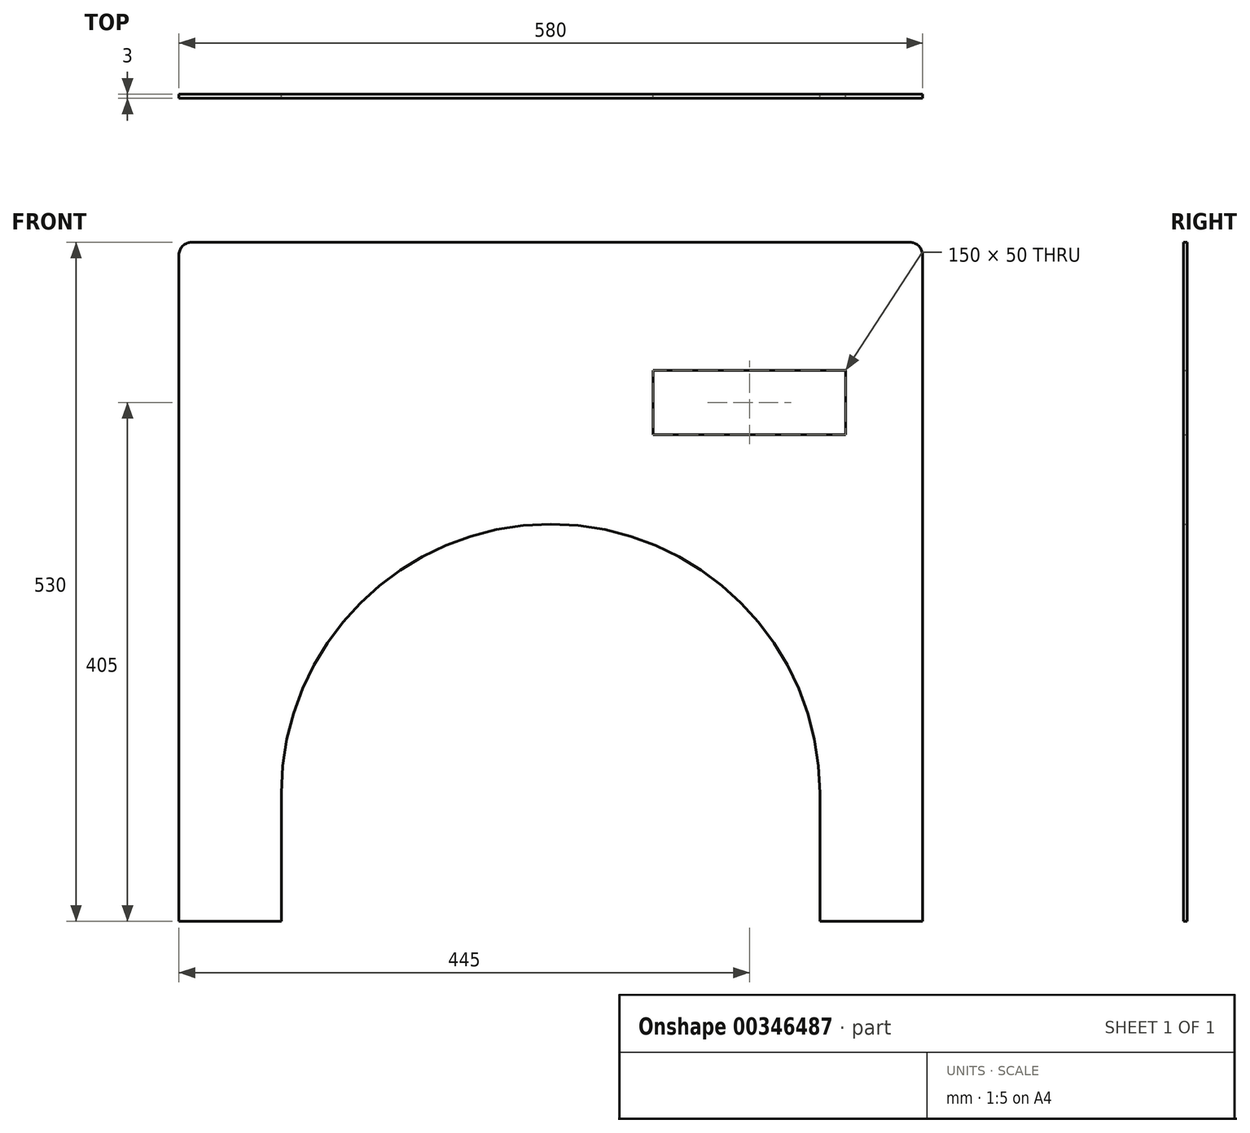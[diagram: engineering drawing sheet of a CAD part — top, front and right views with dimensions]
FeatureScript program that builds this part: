
annotation { "Feature Type Name" : "Feature", "Feature Type Description" : "" }
export const myFeature = defineFeature(function(context is Context, id is Id, definition is map)
    precondition{}
    {
        {
            var Q0;
            Q0=qCreatedBy(makeId("Front.planeOp"),FACE);
            var sketch = newSketch(context, id + "F0", { "sketchPlane" : qUnion([Q0])});
            skLineSegment(sketch, "E0", {"start": v(-280, 430) * mm, "end": v(280, 430) * mm});
            skLineSegment(sketch, "E1", {"start": v(290, 420) * mm, "end": v(290, -100) * mm});
            skLineSegment(sketch, "E2", {"start": v(290, -100) * mm, "end": v(210, -100) * mm});
            skLineSegment(sketch, "E3", {"start": v(-290, -100) * mm, "end": v(-290, 420) * mm});
            skPoint(sketch, "E4", {"position": v(-210, -100) * mm});
            skPoint(sketch, "E5", {"position": v(210, -100) * mm});
            skLineSegment(sketch, "E6.trimOffspring", {"start": v(-210, -100) * mm, "end": v(-290, -100) * mm});
            skLineSegment(sketch, "E7.top", {"start": v(80, 280) * mm, "end": v(230, 280) * mm});
            skLineSegment(sketch, "E7.left", {"start": v(80, 329.97) * mm, "end": v(80, 280) * mm});
            skLineSegment(sketch, "E7.right", {"start": v(230, 330) * mm, "end": v(230, 280) * mm});
            skPoint(sketch, "E8", {"position": v(80, 329.97) * mm});
            skPoint(sketch, "E9.visualSharp", {"position": v(-290, 430) * mm});
            skArc(sketch, "E9.filletArc", {"start": v(-280, 430) * mm, "mid": v(-287.07, 427.07) * mm, "end": v(-290, 420) * mm});
            skPoint(sketch, "E10.visualSharp", {"position": v(290, 430) * mm});
            skArc(sketch, "E10.filletArc", {"start": v(290, 420) * mm, "mid": v(287.07, 427.07) * mm, "end": v(280, 430) * mm});
            skPoint(sketch, "E11.center.orphan", {"position": v(0, -100) * mm});
            skPoint(sketch, "E12.endSnap0", {"position": v(0.1, 171.57) * mm});
            skPoint(sketch, "E12.end.orphan", {"position": v(0.1, 180.62) * mm});
            skPoint(sketch, "E13.end.orphan", {"position": v(85.62, 0) * mm});
            skPoint(sketch, "E14.start.orphan", {"position": v(-85.41, 0) * mm});
            skPoint(sketch, "E15.end.orphan", {"position": v(-11.25, -100) * mm});
            skPoint(sketch, "E15.start.orphan", {"position": v(-11.25, 211) * mm});
            skLineSegment(sketch, "E16", {"start": v(0.1, 210) * mm, "end": v(0.1, 211) * mm});
            skArc(sketch, "E17", {"start": v(210, 0) * mm, "mid": v(0, 210) * mm, "end": v(-210, 0) * mm});
            skLineSegment(sketch, "E18", {"start": v(-210, 0) * mm, "end": v(-210, -100) * mm});
            skLineSegment(sketch, "E19", {"start": v(210, 0) * mm, "end": v(210, -100) * mm});
            skPoint(sketch, "E20.orphan", {"position": v(80, 379.93) * mm});
            skLineSegment(sketch, "E21", {"start": v(80, 329.97) * mm, "end": v(230, 330) * mm});
            skPoint(sketch, "E22.orphan", {"position": v(230, 380) * mm});
            skPoint(sketch, "E23.endSnap0", {"position": v(80, 304.98) * mm});
            skPoint(sketch, "E23.end.orphan", {"position": v(147.38, 304.98) * mm});
            skSolve(sketch);
        }
        {
            var Q0;
            Q0 = qSketchRegion(id + "F0", true);
            extrude(context, id + "F1", {"entities" : qUnion([Q0]), "depth" : 3 * mm});
        }
    });
